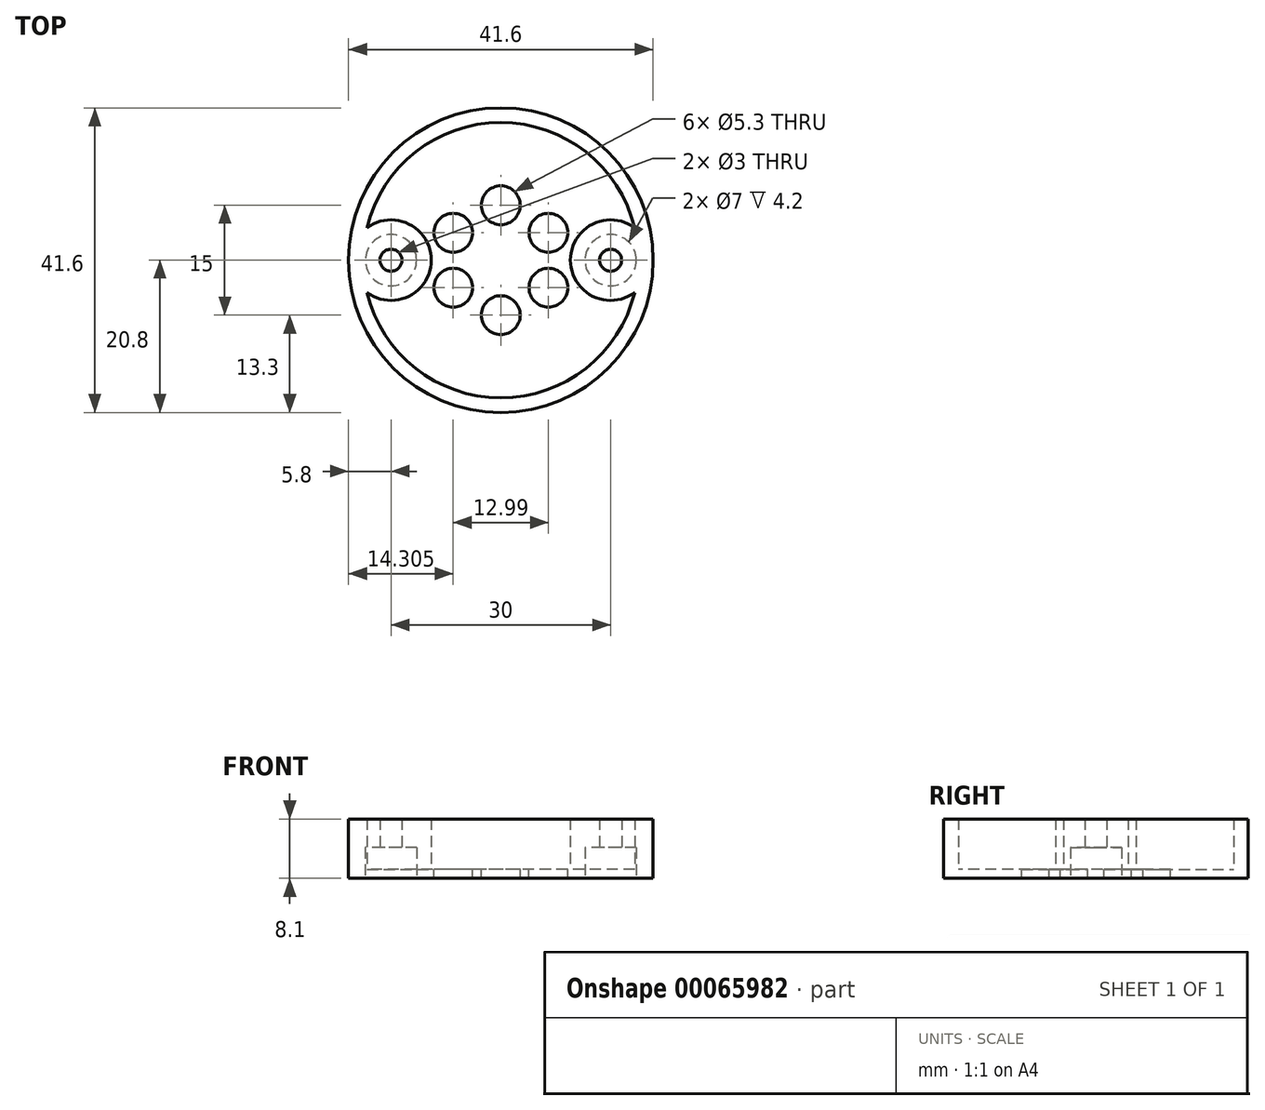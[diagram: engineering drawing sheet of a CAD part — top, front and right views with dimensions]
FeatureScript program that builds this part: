
annotation { "Feature Type Name" : "Feature", "Feature Type Description" : "" }
export const myFeature = defineFeature(function(context is Context, id is Id, definition is map)
    precondition{}
    {
        {
            var Q0;
            Q0=qCreatedBy(makeId("Top.planeOp"),FACE);
            var sketch = newSketch(context, id + "F0", { "sketchPlane" : qUnion([Q0])});
            skLineSegment(sketch, "E0.bottom", {"start": v(0, 0) * mm, "end": v(41.6, 0) * mm, "construction": true});
            skLineSegment(sketch, "E0.top", {"start": v(0, 41.6) * mm, "end": v(41.6, 41.6) * mm, "construction": true});
            skLineSegment(sketch, "E0.left", {"start": v(0, 0) * mm, "end": v(0, 41.6) * mm, "construction": true});
            skLineSegment(sketch, "E0.right", {"start": v(41.6, 0) * mm, "end": v(41.6, 41.6) * mm, "construction": true});
            skCircle(sketch, "E1", {"center": v(20.8, 20.8) * mm, "radius": 20.8 * mm});
            skCircle(sketch, "E2", {"center": v(5.8, 20.8) * mm, "radius": 3.5 * mm});
            skPoint(sketch, "E2.centerSnap0", {"position": v(0, 20.8) * mm});
            skCircle(sketch, "E3", {"center": v(35.8, 20.8) * mm, "radius": 3.5 * mm});
            skSolve(sketch);
        }
        {
            var Q0;
            Q0=qSketchRegion(id+"F0",true);
            extrude(context, id + "F1", {"entities" : qUnion([Q0]), "depth" : 1.2 * mm});
        }
        {
            var Q0;
            Q0=makeQuery(id+"F1.opExtrude","CAP_FACE",FACE,{"disambiguationData":[OSD([sQuery(id+"F0.wireOp",EDGE,"E1")])],"isStart":false});
            var sketch = newSketch(context, id + "F2", { "sketchPlane" : qUnion([Q0])});
            skCircle(sketch, "E4", {"center": v(20.8, 20.8) * mm, "radius": 20.8 * mm});
            skCircle(sketch, "E5", {"center": v(5.8, 20.8) * mm, "radius": 3.5 * mm});
            skCircle(sketch, "E6", {"center": v(35.8, 20.8) * mm, "radius": 3.5 * mm});
            skArc(sketch, "E7", {"start": v(2.53, 16.38) * mm, "mid": v(11.3, 20.8) * mm, "end": v(2.53, 25.22) * mm});
            skArc(sketch, "E8", {"start": v(39.07, 16.38) * mm, "mid": v(30.3, 20.8) * mm, "end": v(39.07, 25.22) * mm});
            skArc(sketch, "E9", {"start": v(2.53, 25.22) * mm, "mid": v(20.8, 39.6) * mm, "end": v(39.07, 25.22) * mm});
            skArc(sketch, "E10", {"start": v(2.53, 16.38) * mm, "mid": v(20.8, 2) * mm, "end": v(39.07, 16.38) * mm});
            skSolve(sketch);
        }
        {
            var Q0;
            Q0 = qSketchRegion(id + "F2", true);
            extrude(context, id + "F3", {"entities" : qUnion([Q0]), "operationType" : NewBodyOperationType.ADD, "depth" : 3 * mm});
        }
        {
            var Q0;
            Q0=makeQuery(id+"F3.opExtrude","CAP_FACE",FACE,{"disambiguationData":[OSD([sQuery(id+"F2.wireOp",EDGE,"E4"),sQuery(id+"F2.wireOp",EDGE,"E5"),sQuery(id+"F2.wireOp",EDGE,"E6"),sQuery(id+"F2.wireOp",EDGE,"E7"),sQuery(id+"F2.wireOp",EDGE,"E8"),sQuery(id+"F2.wireOp",EDGE,"E9"),sQuery(id+"F2.wireOp",EDGE,"E10")])],"isStart":false});
            var sketch = newSketch(context, id + "F4", { "sketchPlane" : qUnion([Q0])});
            skCircle(sketch, "E11", {"center": v(20.8, 20.8) * mm, "radius": 20.8 * mm});
            skCircle(sketch, "E12", {"center": v(5.8, 20.8) * mm, "radius": 1.5 * mm});
            skCircle(sketch, "E13", {"center": v(35.8, 20.8) * mm, "radius": 1.5 * mm});
            skArc(sketch, "E14", {"start": v(2.53, 16.38) * mm, "mid": v(11.3, 20.8) * mm, "end": v(2.53, 25.22) * mm});
            skArc(sketch, "E15", {"start": v(39.07, 16.38) * mm, "mid": v(30.3, 20.8) * mm, "end": v(39.07, 25.22) * mm});
            skArc(sketch, "E16", {"start": v(2.53, 16.38) * mm, "mid": v(20.8, 2) * mm, "end": v(39.07, 16.38) * mm});
            skArc(sketch, "E17", {"start": v(39.07, 25.22) * mm, "mid": v(20.8, 39.6) * mm, "end": v(2.53, 25.22) * mm});
            skSolve(sketch);
        }
        {
            var Q0;
            Q0 = qSketchRegion(id + "F4", true);
            extrude(context, id + "F5", {"entities" : qUnion([Q0]), "operationType" : NewBodyOperationType.ADD, "depth" : 3.9 * mm});
        }
        {
            var Q0;
            Q0=makeQuery(id+"F1.opExtrude","CAP_FACE",FACE,{"disambiguationData":[OSD([sQuery(id+"F0.wireOp",EDGE,"E1"),sQuery(id+"F0.wireOp",EDGE,"E2"),sQuery(id+"F0.wireOp",EDGE,"E3")])],"isStart":false});
            var sketch = newSketch(context, id + "F6", { "sketchPlane" : qUnion([Q0])});
            skCircle(sketch, "E18.cCircle", {"center": v(20.8, 20.8) * mm, "radius": 7.5 * mm, "construction": true});
            skLineSegment(sketch, "E18.0", {"start": v(20.8, 13.3) * mm, "end": v(14.3, 17.05) * mm, "construction": true});
            skLineSegment(sketch, "E18.1", {"start": v(14.3, 17.05) * mm, "end": v(14.3, 24.55) * mm, "construction": true});
            skLineSegment(sketch, "E18.2", {"start": v(14.3, 24.55) * mm, "end": v(20.8, 28.3) * mm, "construction": true});
            skLineSegment(sketch, "E18.3", {"start": v(20.8, 28.3) * mm, "end": v(27.3, 24.55) * mm, "construction": true});
            skLineSegment(sketch, "E18.4", {"start": v(27.3, 24.55) * mm, "end": v(27.3, 17.05) * mm, "construction": true});
            skLineSegment(sketch, "E18.5", {"start": v(27.3, 17.05) * mm, "end": v(20.8, 13.3) * mm, "construction": true});
            skCircle(sketch, "E19", {"center": v(14.3, 24.55) * mm, "radius": 2.65 * mm});
            skCircle(sketch, "E20", {"center": v(20.8, 28.3) * mm, "radius": 2.65 * mm});
            skCircle(sketch, "E21", {"center": v(27.3, 24.55) * mm, "radius": 2.65 * mm});
            skCircle(sketch, "E22", {"center": v(27.3, 17.05) * mm, "radius": 2.65 * mm});
            skCircle(sketch, "E23", {"center": v(20.8, 13.3) * mm, "radius": 2.65 * mm});
            skCircle(sketch, "E24", {"center": v(14.3, 17.05) * mm, "radius": 2.65 * mm});
            skSolve(sketch);
        }
        {
            var Q0;
            Q0 = qSketchRegion(id + "F6", true);
            var Q1;
            Q1=makeQuery(id+"F1.opExtrude","CAP_FACE",FACE,{"disambiguationData":[OSD([sQuery(id+"F0.wireOp",EDGE,"E1"),sQuery(id+"F0.wireOp",EDGE,"E2"),sQuery(id+"F0.wireOp",EDGE,"E3")])],"isStart":true});
            extrude(context, id + "F7", {"entities" : qUnion([Q0]), "operationType" : NewBodyOperationType.REMOVE, "endBound" : BoundingType.UP_TO_SURFACE, "oppositeDirection" : true, "endBoundEntityFace" : qUnion([Q1]), "depth" : 25 * mm});
        }
    });
